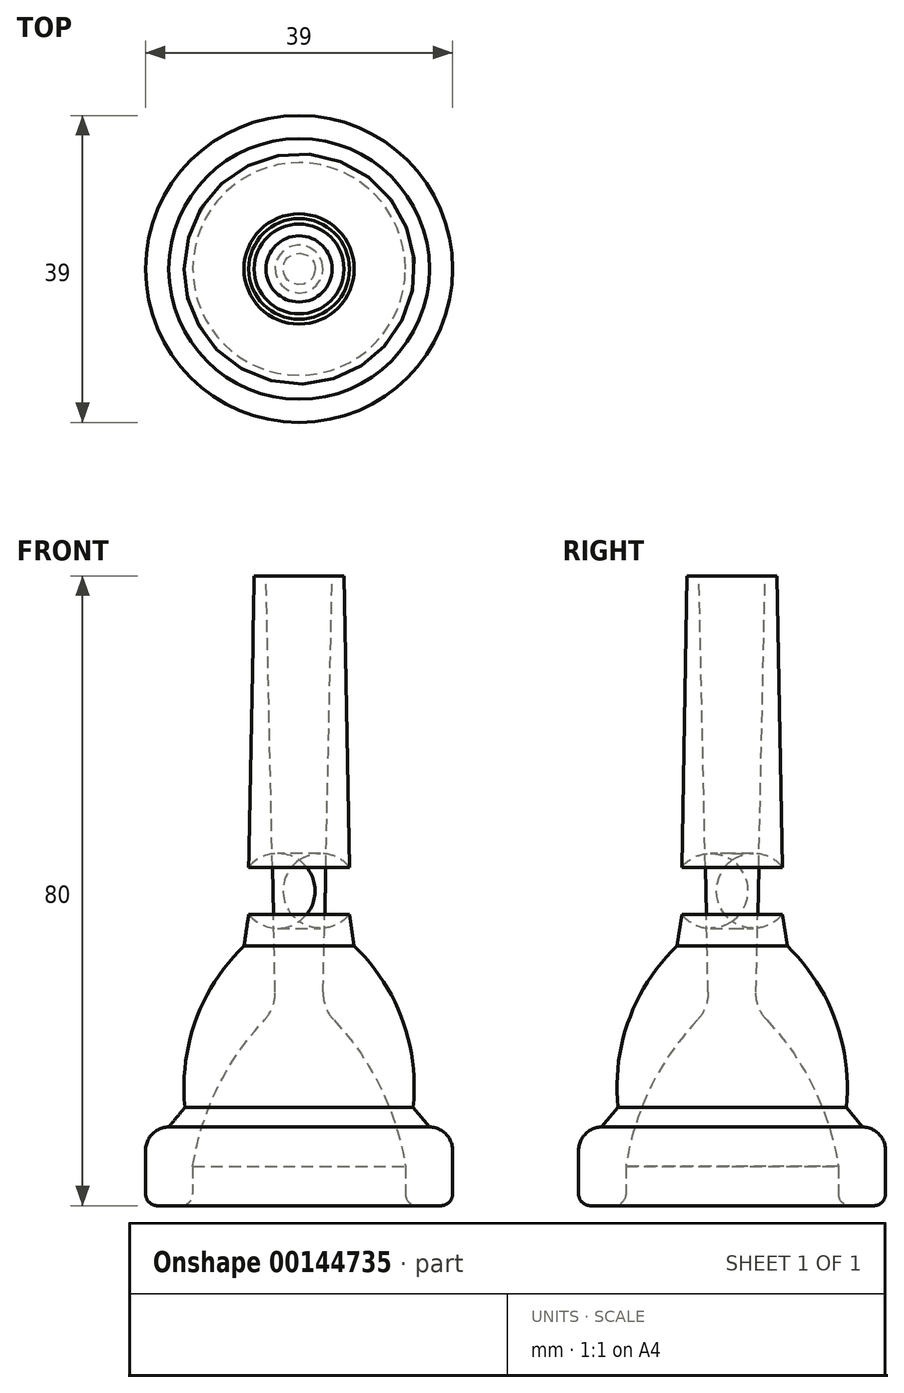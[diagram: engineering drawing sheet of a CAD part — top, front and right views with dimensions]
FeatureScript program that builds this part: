
annotation { "Feature Type Name" : "Feature", "Feature Type Description" : "" }
export const myFeature = defineFeature(function(context is Context, id is Id, definition is map)
    precondition{}
    {
        {
            var Q0;
            Q0=qCreatedBy(makeId("Front.planeOp"),FACE);
            var sketch = newSketch(context, id + "F0", { "sketchPlane" : qUnion([Q0])});
            skArc(sketch, "E0", {"start": v(-5.34, -62.83) * mm, "mid": v(-6.73, -51.72) * mm, "end": v(-12.84, -42.33) * mm});
            skLineSegment(sketch, "E1", {"start": v(-5.34, -62.83) * mm, "end": v(-3.28, -65.33) * mm});
            skLineSegment(sketch, "E2", {"start": v(-3.28, -65.33) * mm, "end": v(-0.34, -65.33) * mm});
            skLineSegment(sketch, "E3", {"start": v(-0.34, -65.33) * mm, "end": v(-0.34, -75.33) * mm});
            skLineSegment(sketch, "E4", {"start": v(-19.84, -75.33) * mm, "end": v(-19.84, 4.67) * mm});
            skLineSegment(sketch, "E5", {"start": v(-14.14, 4.67) * mm, "end": v(-13.44, -32.33) * mm});
            skLineSegment(sketch, "E6", {"start": v(-13.44, -38.33) * mm, "end": v(-12.84, -42.33) * mm});
            skArc(sketch, "E7", {"start": v(-13.44, -38.33) * mm, "mid": v(-12.37, -35.33) * mm, "end": v(-13.44, -32.33) * mm});
            skLineSegment(sketch, "E8", {"start": v(-19.84, 4.67) * mm, "end": v(-14.14, 4.67) * mm});
            skLineSegment(sketch, "E9", {"start": v(-19.84, -75.33) * mm, "end": v(-0.34, -75.33) * mm});
            skLineSegment(sketch, "E10", {"start": v(-15.64, 4.67) * mm, "end": v(-16.84, -50.33) * mm});
            skLineSegment(sketch, "E11", {"start": v(-6.34, -75.33) * mm, "end": v(-6.34, -70.33) * mm});
            skArc(sketch, "E12", {"start": v(-6.34, -70.33) * mm, "mid": v(-9.93, -59.46) * mm, "end": v(-16.84, -50.33) * mm});
            skSolve(sketch);
        }
        {
            var Q0;
            Q0=makeQuery(id+"F0.imprint","IMPRINT",FACE,{"disambiguationData":[TD([[makeQuery(id+"F0.imprint","IMPRINT",EDGE,{"derivedFrom":sQuery(id+"F0.wireOp",EDGE,"E0")}),1.0]])]});
            var Q1;
            Q1=sQuery(id+"F0.wireOp",EDGE,"E4");
            revolve(context, id + "F1", {"entities" : qUnion([Q0]), "axis" : qUnion([Q1]), "revolveType" : RevolveType.FULL});
        }
        {
            var Q0;
            Q0=makeQuery(id+"F1.opRevolve","SWEPT_EDGE",EDGE,{"disambiguationData":[OSD([sQuery(id+"F0.wireOp",EDGE,"E2"),sQuery(id+"F0.wireOp",EDGE,"E3")])]});
            fillet(context, id + "F2", {"entities" : qUnion([Q0]), "radius" : 3 * mm, "tangentPropagation" : true, "allowEdgeOverflow" : false});
        }
        {
            var Q0;
            Q0=makeQuery(id+"F1.opRevolve","SWEPT_EDGE",EDGE,{"disambiguationData":[OSD([sQuery(id+"F0.wireOp",EDGE,"E9"),sQuery(id+"F0.wireOp",EDGE,"E11")])]});
            var Q1;
            Q1=makeQuery(id+"F1.opRevolve","SWEPT_EDGE",EDGE,{"disambiguationData":[OSD([sQuery(id+"F0.wireOp",EDGE,"E3"),sQuery(id+"F0.wireOp",EDGE,"E9")])]});
            fillet(context, id + "F3", {"entities" : qUnion([Q0, Q1]), "radius" : 1.5 * mm, "tangentPropagation" : true, "allowEdgeOverflow" : false});
        }
        {
            var Q0;
            Q0=makeQuery(id+"F1.opRevolve","SWEPT_EDGE",EDGE,{"disambiguationData":[OSD([sQuery(id+"F0.wireOp",EDGE,"E10"),sQuery(id+"F0.wireOp",EDGE,"E12")])]});
            fillet(context, id + "F4", {"entities" : qUnion([Q0]), "radius" : 5 * mm, "tangentPropagation" : true, "allowEdgeOverflow" : false});
        }
    });
